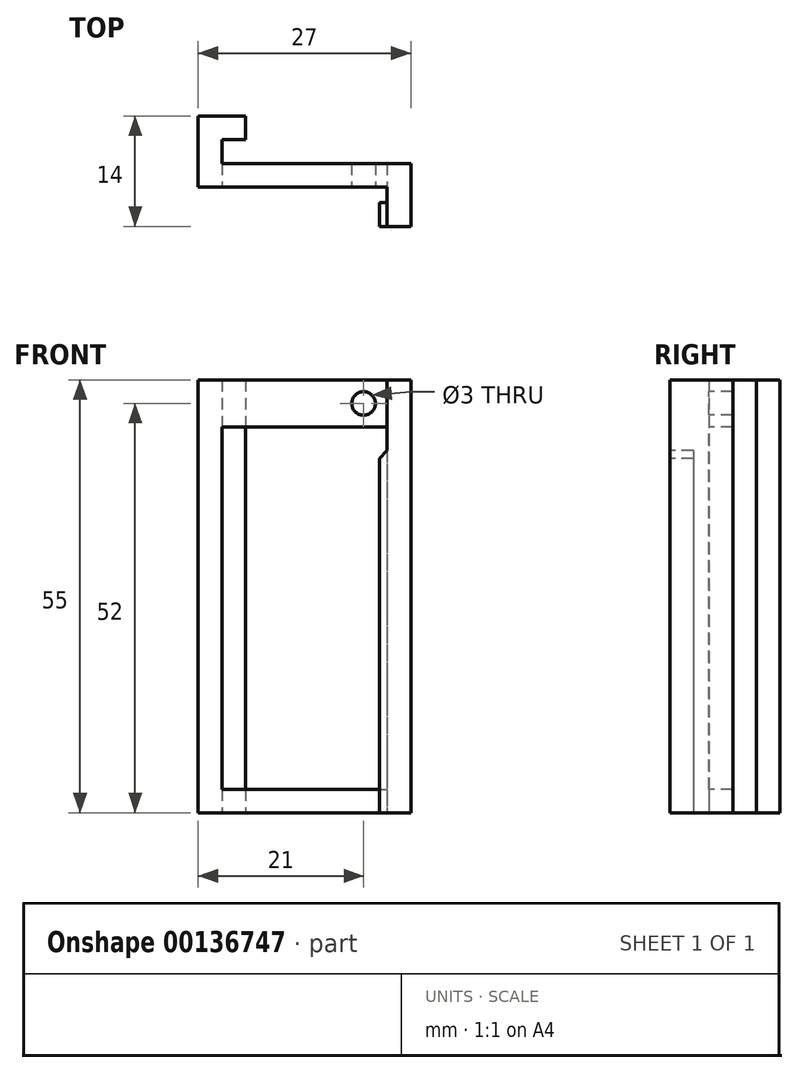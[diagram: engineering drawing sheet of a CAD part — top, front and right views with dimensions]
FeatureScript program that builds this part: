
annotation { "Feature Type Name" : "Feature", "Feature Type Description" : "" }
export const myFeature = defineFeature(function(context is Context, id is Id, definition is map)
    precondition{}
    {
        {
            var Q0;
            Q0=qCreatedBy(makeId("Top.planeOp"),FACE);
            var sketch = newSketch(context, id + "F0", { "sketchPlane" : qUnion([Q0])});
            skLineSegment(sketch, "E0", {"start": v(0, 0) * mm, "end": v(0, 3) * mm});
            skLineSegment(sketch, "E1", {"start": v(0, 3) * mm, "end": v(3, 3) * mm});
            skLineSegment(sketch, "E2", {"start": v(3, 3) * mm, "end": v(3, 6) * mm});
            skLineSegment(sketch, "E3", {"start": v(3, 6) * mm, "end": v(-3, 6) * mm});
            skLineSegment(sketch, "E4", {"start": v(-3, 6) * mm, "end": v(-3, -3) * mm});
            skLineSegment(sketch, "E5", {"start": v(-3, -3) * mm, "end": v(21, -3) * mm});
            skLineSegment(sketch, "E6", {"start": v(21, -3) * mm, "end": v(21, -5) * mm});
            skLineSegment(sketch, "E7", {"start": v(21, -5) * mm, "end": v(20, -5) * mm});
            skLineSegment(sketch, "E8", {"start": v(20, -5) * mm, "end": v(20, -8) * mm});
            skLineSegment(sketch, "E9", {"start": v(20, -8) * mm, "end": v(24, -8) * mm});
            skLineSegment(sketch, "E10", {"start": v(24, -8) * mm, "end": v(24, 0) * mm});
            skLineSegment(sketch, "E11", {"start": v(24, 0) * mm, "end": v(0, 0) * mm});
            skSolve(sketch);
        }
        {
            var Q0;
            Q0=makeQuery(id+"F0.imprint","IMPRINT",FACE,{"disambiguationData":[TD([[makeQuery(id+"F0.imprint","IMPRINT",EDGE,{"derivedFrom":sQuery(id+"F0.wireOp",EDGE,"E0")}),1.0]])]});
            extrude(context, id + "F1", {"entities" : qUnion([Q0]), "depth" : 55 * mm});
        }
        {
            var Q0;
            Q0=makeQuery(id+"F1.opExtrude","SWEPT_FACE",FACE,{"disambiguationData":[OSD([sQuery(id+"F0.wireOp",EDGE,"E5")])]});
            var sketch = newSketch(context, id + "F2", { "sketchPlane" : qUnion([Q0])});
            skCircle(sketch, "E12", {"center": v(18, 52) * mm, "radius": 1.5 * mm});
            skLineSegment(sketch, "E13.bottom", {"start": v(0, 3) * mm, "end": v(21, 3) * mm});
            skLineSegment(sketch, "E13.top", {"start": v(0, 49) * mm, "end": v(21, 49) * mm});
            skLineSegment(sketch, "E13.left", {"start": v(0, 3) * mm, "end": v(0, 49) * mm});
            skLineSegment(sketch, "E13.right", {"start": v(21, 3) * mm, "end": v(21, 49) * mm});
            skSolve(sketch);
        }
        {
            var Q0;
            Q0=makeQuery(id+"F2.imprint","IMPRINT",FACE,{"disambiguationData":[TD([[makeQuery(id+"F2.imprint","IMPRINT",EDGE,{"derivedFrom":sQuery(id+"F2.wireOp",EDGE,"E12")}),1.0]])]});
            var Q1;
            Q1=makeQuery(id+"F2.imprint","IMPRINT",FACE,{"disambiguationData":[TD([[makeQuery(id+"F2.imprint","IMPRINT",EDGE,{"derivedFrom":sQuery(id+"F2.wireOp",EDGE,"E13.bottom")}),1.0]])]});
            extrude(context, id + "F3", {"entities" : qUnion([Q0, Q1]), "operationType" : NewBodyOperationType.REMOVE, "oppositeDirection" : true, "depth" : 5 * mm});
        }
        {
            var Q0;
            Q0=makeQuery(id+"F1.opExtrude","SWEPT_FACE",FACE,{"disambiguationData":[OSD([sQuery(id+"F0.wireOp",EDGE,"E8")])]});
            var sketch = newSketch(context, id + "F4", { "sketchPlane" : qUnion([Q0])});
            skLineSegment(sketch, "E14.bottom", {"start": v(5, 55) * mm, "end": v(8, 55) * mm});
            skLineSegment(sketch, "E14.top", {"start": v(5, 45) * mm, "end": v(8, 45) * mm});
            skLineSegment(sketch, "E14.left", {"start": v(5, 55) * mm, "end": v(5, 45) * mm});
            skLineSegment(sketch, "E14.right", {"start": v(8, 55) * mm, "end": v(8, 45) * mm});
            skSolve(sketch);
        }
        {
            var Q0;
            Q0=makeQuery(id+"F4.imprint","IMPRINT",FACE,{"disambiguationData":[TD([[makeQuery(id+"F4.imprint","IMPRINT",EDGE,{"derivedFrom":sQuery(id+"F4.wireOp",EDGE,"E14.bottom")}),-1.0]])]});
            extrude(context, id + "F5", {"entities" : qUnion([Q0]), "operationType" : NewBodyOperationType.REMOVE, "oppositeDirection" : true, "depth" : 1 * mm});
        }
        {
            var Q0;
            Q0=makeQuery(id+"F5.boolean.opBoolean","COPY",EDGE,{"derivedFrom":makeQuery(id+"F5.opExtrude","CAP_EDGE",EDGE,{"disambiguationData":[OSD([sQuery(id+"F4.wireOp",EDGE,"E14.top")])],"isStart":false})});
            chamfer(context, id + "F6", {"entities" : qUnion([Q0]), "width" : 1 * mm, "tangentPropagation" : true});
        }
    });
